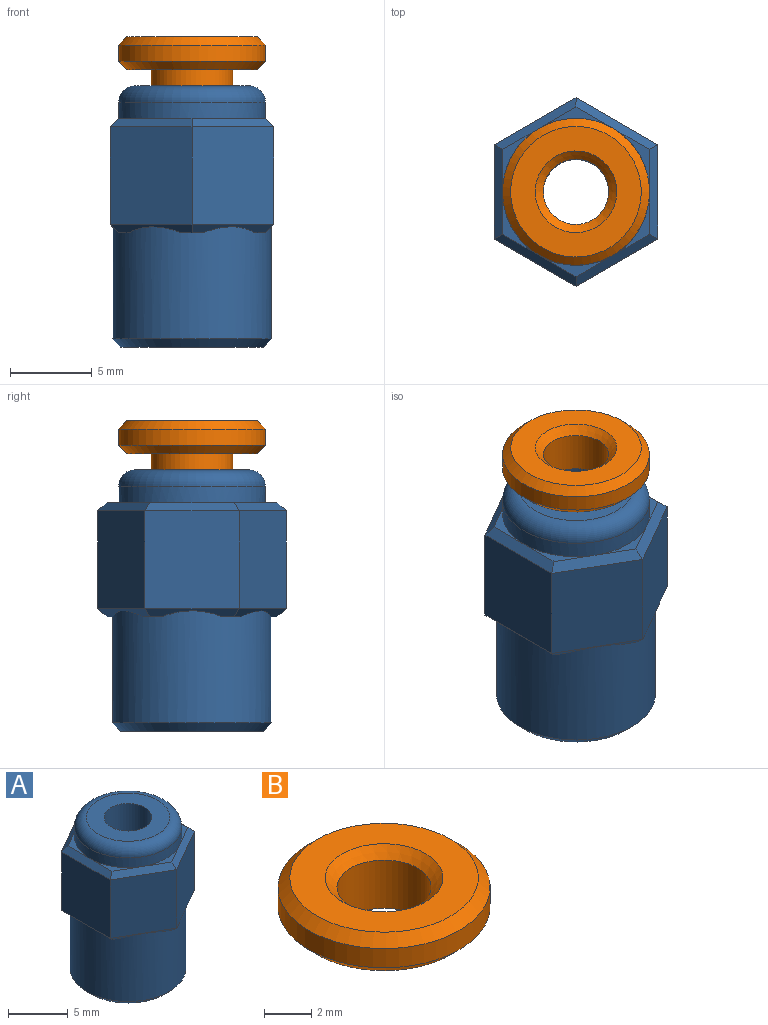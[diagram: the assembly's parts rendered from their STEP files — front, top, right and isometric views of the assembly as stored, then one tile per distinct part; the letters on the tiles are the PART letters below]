
ASSEMBLY  parts=2 mates=1
PART A: 38 faces, bbox 10x11.5x16 mm
  f0: plane 3.9x2.25mm, normal (0,0,1), area 1.1mm2, adj f20,f36,f37
  f1: plane 3.9x2.25mm, normal (0,0,1), area 1.1mm2, adj f20,f35,f37
  f2: plane 4.5x1.3mm, normal (0,0,1), area 1.1mm2, adj f20,f33,f35
  f3: plane 3.9x2.25mm, normal (0,0,1), area 1.1mm2, adj f20,f32,f33
  f4: plane 3.9x2.25mm, normal (0,0,1), area 1.1mm2, adj f20,f32,f34
  f5: plane 1.3x0.38mm, normal (0,0,-1), area 0.2mm2, adj f10,f29,f31
  f6: plane 1.13x0.65mm, normal (0,0,-1), area 0.2mm2, adj f10,f27,f29
  f7: plane 1.13x0.65mm, normal (0,0,-1), area 0.2mm2, adj f10,f26,f27
  f8: plane 1.3x0.38mm, normal (0,0,-1), area 0.2mm2, adj f10,f26,f28
  f9: plane 1.13x0.65mm, normal (0,0,-1), area 0.2mm2, adj f10,f30,f31
  f10: cylinder r=4.86mm len=9.73mm, axis (0,0,1), area 204.1mm2, adj f5,f6,f7,f8,f9,f19,f25,f26
  f11: plane 8.73x8.73mm, normal (0,0,-1), area 40.2mm2, adj f24,f25
  f12: plane 6x5.77mm, normal (-1,0,0), area 34.6mm2, adj f13,f17,f30,f37
  f13: plane 6x5mm, normal (-0.5,-0.87,0), area 34.6mm2, adj f12,f14,f31,f35
  f14: plane 6x5mm, normal (0.5,-0.87,0), area 34.6mm2, adj f13,f15,f29,f33
  f15: plane 6x5.77mm, normal (1,0,0), area 34.6mm2, adj f14,f16,f27,f32
  f16: plane 6x5mm, normal (0.5,0.87,0), area 34.6mm2, adj f15,f17,f26,f34
  f17: plane 6x5mm, normal (-0.5,0.87,0), area 34.6mm2, adj f12,f16,f28,f36
  f18: plane 4.5x1.3mm, normal (0,0,1), area 1.1mm2, adj f20,f34,f36
  f19: plane 1.13x0.65mm, normal (0,0,-1), area 0.2mm2, adj f10,f28,f30
  f20: cylinder r=4.5mm len=9mm, axis (0,0,-1), area 28.3mm2, adj f0,f1,f2,f3,f4,f18,f23
  f21: plane 7x7mm, normal (0,0,1), area 25.9mm2, adj f22,f23
  f22: cylinder r=2mm len=15.5mm, axis (0,0,1), area 194.8mm2, adj f21,f24
  f23: torus R=3.5mm, axis (0,0,1), area 40.8mm2, adj f20,f21
  f24: cone r=2.5mm half-angle=45deg, axis (0,0,-1), area 10mm2, adj f11,f22
  f25: cone r=4.86mm half-angle=45deg, axis (0,0,1), area 20.5mm2, adj f10,f11
  f26: plane 5x3.18mm, normal (0.35,0.61,-0.71), area 2.6mm2, adj f7,f8,f10,f16,f27,f28
  f27: plane 5.77x0.5mm, normal (0.71,0,-0.71), area 2.6mm2, adj f6,f7,f10,f15,f26,f29
  f28: plane 5x3.18mm, normal (-0.35,0.61,-0.71), area 2.6mm2, adj f8,f10,f17,f19,f26,f30
  f29: plane 5x3.18mm, normal (0.35,-0.61,-0.71), area 2.6mm2, adj f5,f6,f10,f14,f27,f31
  f30: plane 5.77x0.5mm, normal (-0.71,0,-0.71), area 2.6mm2, adj f9,f10,f12,f19,f28,f31
  f31: plane 5x3.18mm, normal (-0.35,-0.61,-0.71), area 2.6mm2, adj f5,f9,f10,f13,f29,f30
  f32: plane 5.77x0.5mm, normal (0.71,0,0.71), area 3.9mm2, adj f3,f4,f15,f33,f34
  f33: plane 5x3.18mm, normal (0.35,-0.61,0.71), area 3.9mm2, adj f2,f3,f14,f32,f35
  f34: plane 5x3.18mm, normal (0.35,0.61,0.71), area 3.9mm2, adj f4,f16,f18,f32,f36
  f35: plane 5x3.18mm, normal (-0.35,-0.61,0.71), area 3.9mm2, adj f1,f2,f13,f33,f37
  f36: plane 5x3.18mm, normal (-0.35,0.61,0.71), area 3.9mm2, adj f0,f17,f18,f34,f37
  f37: plane 5.77x0.5mm, normal (-0.71,0,0.71), area 3.9mm2, adj f0,f1,f12,f35,f36
PART B: 9 faces, bbox 9x9x3 mm
  f0: cylinder r=2.5mm len=5mm, axis (0,0,-1), area 15.7mm2, adj f1,f4
  f1: plane 5x5mm, normal (0,0,-1), area 7.1mm2, adj f0,f5
  f2: cylinder r=4.5mm len=9mm, axis (0,0,-1), area 28.3mm2, adj f6,f8
  f3: plane 8x8mm, normal (0,0,1), area 30.6mm2, adj f7,f8
  f4: plane 8x8mm, normal (0,0,-1), area 30.6mm2, adj f0,f6
  f5: cylinder r=2mm len=4mm, axis (0,0,1), area 31.4mm2, adj f1,f7
  f6: cone r=4.5mm half-angle=45deg, axis (0,0,1), area 18.9mm2, adj f2,f4
  f7: cone r=2mm half-angle=45deg, axis (0,0,1), area 10mm2, adj f3,f5
  f8: cone r=4mm half-angle=45deg, axis (0,0,-1), area 18.9mm2, adj f2,f3
PLACE A at identity fixed
PLACE B at identity
MATE fastened B.f5 <-> A.f10  axis (0,0,-1) through (0,0,9)mm
